# Revit family: Турникет трипод PERCo_TTR-04, 07
name_source: partatom
category: Оборудование
units: mm (PartAtom-declared; Revit-internal decimal feet)

## family parameters
Всегда вертикально = Да
Классификация = Нет
На основе рабочей плоскости = Нет
Общий = Нет
При загрузке вырезать с полостями = Нет
Размер круглого соединителя = Использовать диаметр
Тип детали = Нормальный
Точка расчета площади = Нет

## types (3) — shared parameters
ADSK_URL страницы изделия = https://www.perco.ru
ADSK_Единица измерения = шт.
ADSK_Завод-изготовитель = PERCo
ADSK_Количество = 1
ADSK_Материал наименование = Корпус из стали, окрашенной порошковой краской. Планки выполнены из нержавеющей стали.
ADSK_Напряжение = 12 В
Встраивание считывателей внутрь = Не предусмотрено
Габаритные размеры контроллера для встраивания в нишу = Не предусмотрено
Габаритные размеры считывателя для встраивания в ниши = Не предусмотрено
Длина планки = 554 мм
Подключение к электросети = 220 В
Пропускная способность = 30 чел./мин

## per-type parameters (varying)
| type | ADSK_Масса_Текст | ADSK_Наименование | ADSK_Номинальная мощность | ADSK_Ток | Габаритные размеры (длина×ширина×высота) | Окраска турникета | Степень защиты оболочки | Температура использования | Цвет | Ширина зоны прохода |
| Турникет TTR-04CW | не более 37 кг | Турникет эл/мех PERCo-TTR-04CW для эксплуатации на открытом воздухе | 9 Вт | 1 А | 855×810×1050 | светло-бежевый с эффектом слюды | IP42 | от –40°С до +50°С | Светло-бежевый с эффектом слюды | 600 мм |
| Турникет TTR-04.1 | не более 30 кг | Турникет эл/мех PERCo-TTR-04.1 для эксплуатации в закрытых помещениях | 9 Вт | 1 А | 855×810×1050 | тёмно-серый с эффектом слюды | IP41 | от +1°С до +50°С | светло-бежевый с эффектом слюды,тёмно-серый с эффектом слюды, чёрный металлик «звездная ночь» | 600 мм |
| Турникет TTR-07.1 | не более 36 кг | Турникет эл/мех PERCo-TTR-07.1G с автоматическими преграждающими планками Антипаника | 72 Вт | 6 А | 798×752×1054 | тёмно-серый с эффектом слюды | IP41 | от +1°С до +50°С | тёмно-серый с эффектом слюды | 530 мм |

note: column(s) folded — value = type name in every type: ADSK_Наименование краткое
